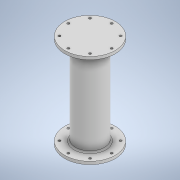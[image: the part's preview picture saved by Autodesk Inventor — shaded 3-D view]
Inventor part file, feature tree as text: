
AUTODESK INVENTOR PART (.ipt)
format: ipt  version: 2021 (Build 250183000, 183)  size: 179,200 bytes
history: native  units: mm
features: sketch x3, revolve x2, projected_geometry x2, hole x1, mirror x1
ambient origin geometry x8: Origin, YZ Plane, XZ Plane, XY Plane, X Axis, Y Axis, Z Axis, Center Point
bodies: Solid1 (feature_tree)
feature tree (9):
  revolve  "Revolution1"  Angle=90.0deg
  revolve  "Revolution2"  [1 undecoded]
  sketch  "Sketch2"  dims[d6=42.5mm d7=60.0mm]
  hole  "Hole2"  [1 undecoded]
  mirror  "Mirror1"
  sketch  "Sketch1"  dims[d2=130.0mm d5=90.0deg]
  projected_geometry  "Projected Loop1"
  sketch  "Sketch4"  dims[d8=80.0mm d10=360.0deg d12=35.0mm d20=3.242mm d21=8.0mm d22=6.5mm d23=3.0mm d24=90.0deg d25=8.0mm d26=20.594885mm d35=20.0mm d36=4.0mm d37=2.0mm d38=90.0deg]
  projected_geometry  "Projected Loop4"
note: 2 required parameter values undecoded (feature->parameter linkage not recoverable at this tier; creation-order binding heuristic only, values carry confidence <= 0.55)